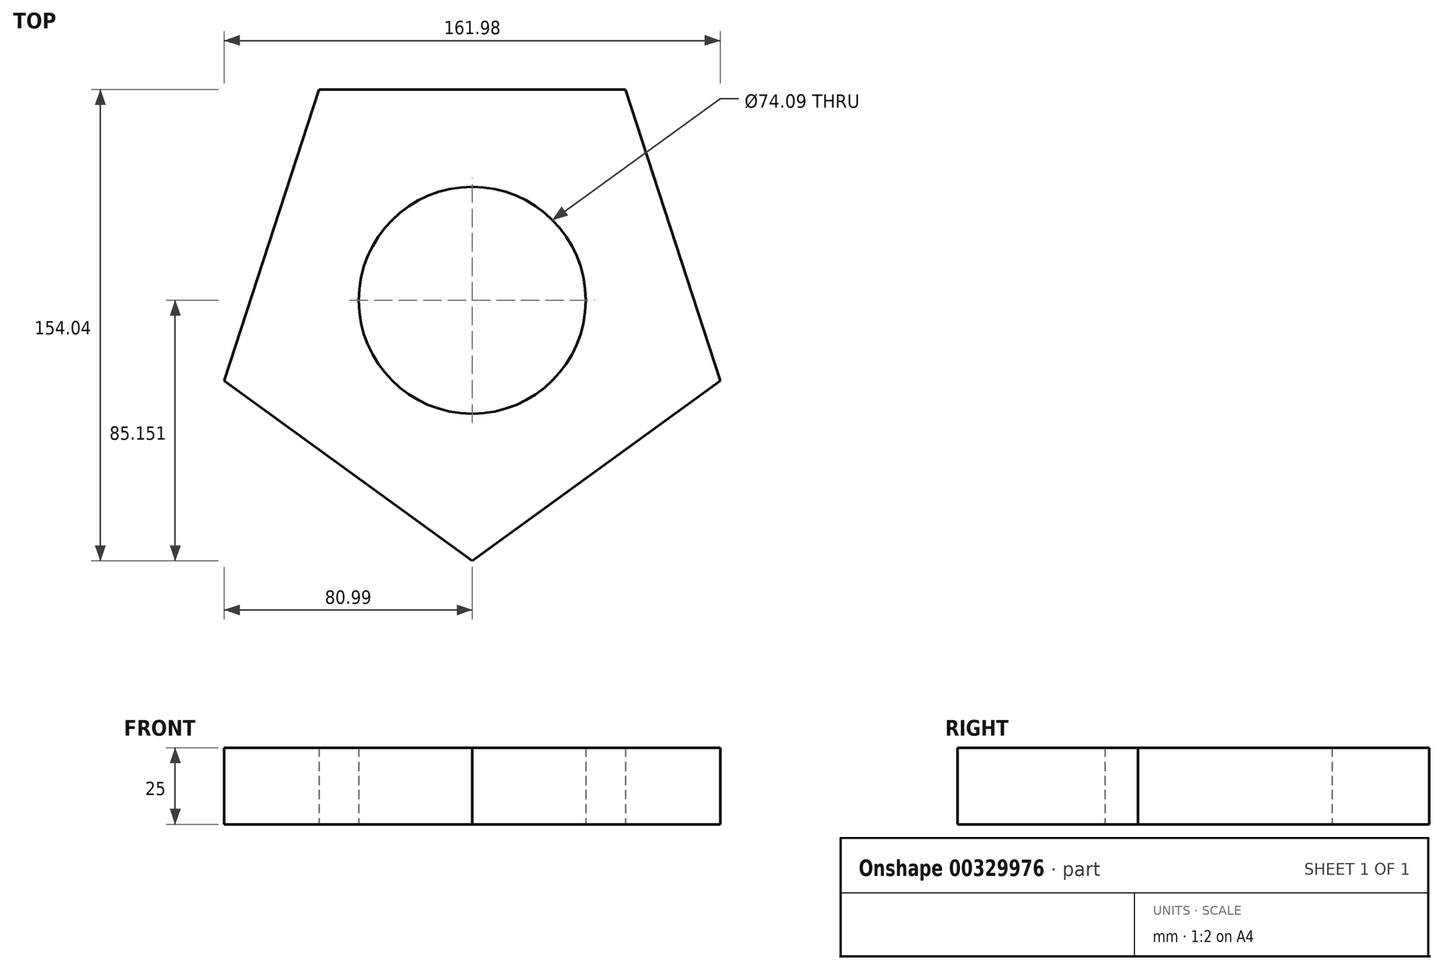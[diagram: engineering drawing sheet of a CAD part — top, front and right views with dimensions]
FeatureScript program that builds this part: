
annotation { "Feature Type Name" : "Feature", "Feature Type Description" : "" }
export const myFeature = defineFeature(function(context is Context, id is Id, definition is map)
    precondition{}
    {
        {
            var Q0;
            Q0=qCreatedBy(makeId("Top.planeOp"),FACE);
            var sketch = newSketch(context, id + "F0", { "sketchPlane" : qUnion([Q0])});
            skCircle(sketch, "E0.cCircle", {"center": v(0, 47.8) * mm, "radius": 85.16 * mm, "construction": true});
            skLineSegment(sketch, "E0.0", {"start": v(0, -37.35) * mm, "end": v(-80.99, 21.49) * mm});
            skLineSegment(sketch, "E0.1", {"start": v(-80.99, 21.49) * mm, "end": v(-50.05, 116.7) * mm});
            skLineSegment(sketch, "E0.2", {"start": v(-50.05, 116.7) * mm, "end": v(50.05, 116.7) * mm});
            skLineSegment(sketch, "E0.3", {"start": v(50.05, 116.7) * mm, "end": v(80.99, 21.49) * mm});
            skLineSegment(sketch, "E0.4", {"start": v(80.99, 21.49) * mm, "end": v(0, -37.35) * mm});
            skCircle(sketch, "E1", {"center": v(0, 47.8) * mm, "radius": 37.04 * mm});
            skSolve(sketch);
        }
        {
            var Q0;
            Q0 = qSketchRegion(id + "F0", true);
            extrude(context, id + "F1", {"entities" : qUnion([Q0]), "depth" : 25 * mm});
        }
    });
